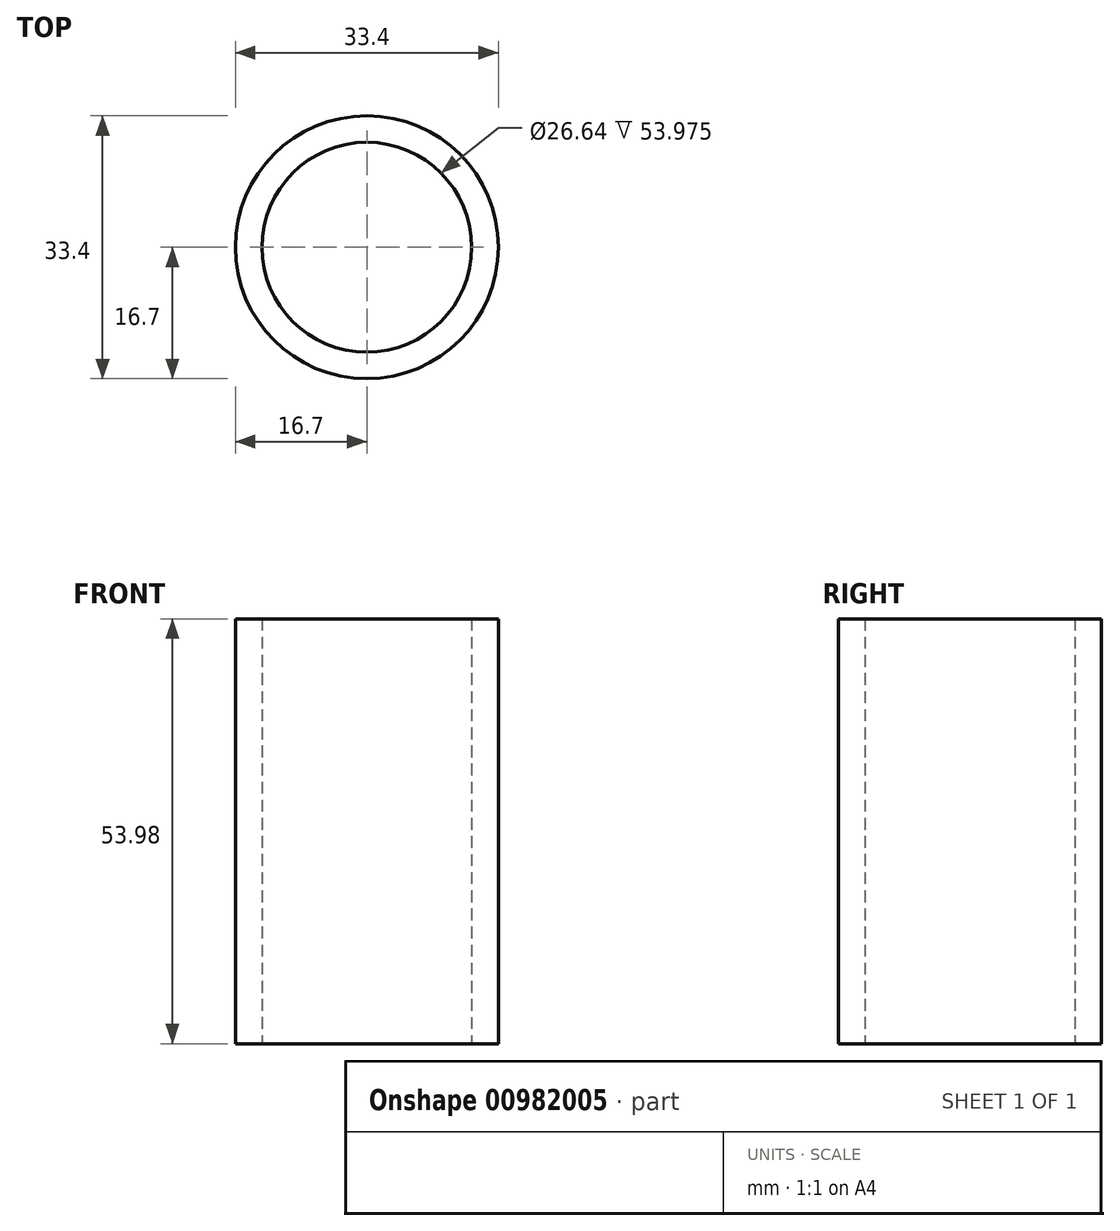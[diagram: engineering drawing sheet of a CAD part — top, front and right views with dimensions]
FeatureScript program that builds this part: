
annotation { "Feature Type Name" : "Feature", "Feature Type Description" : "" }
export const myFeature = defineFeature(function(context is Context, id is Id, definition is map)
    precondition{}
    {
        {
            var Q0;
            Q0=qCreatedBy(makeId("Top.planeOp"),FACE);
            var sketch = newSketch(context, id + "F0", { "sketchPlane" : qUnion([Q0])});
            skCircle(sketch, "E0", {"center": v(0, 0) * mm, "radius": 13.32 * mm});
            skCircle(sketch, "E1", {"center": v(0, 0) * mm, "radius": 16.7 * mm});
            skSolve(sketch);
        }
        {
            var Q0;
            Q0=qSketchRegion(id+"F0",true);
            extrude(context, id + "F1", {"entities" : qUnion([Q0]), "depth" : 53.97 * mm, "offsetDistance" : 25.4 * mm});
        }
    });
